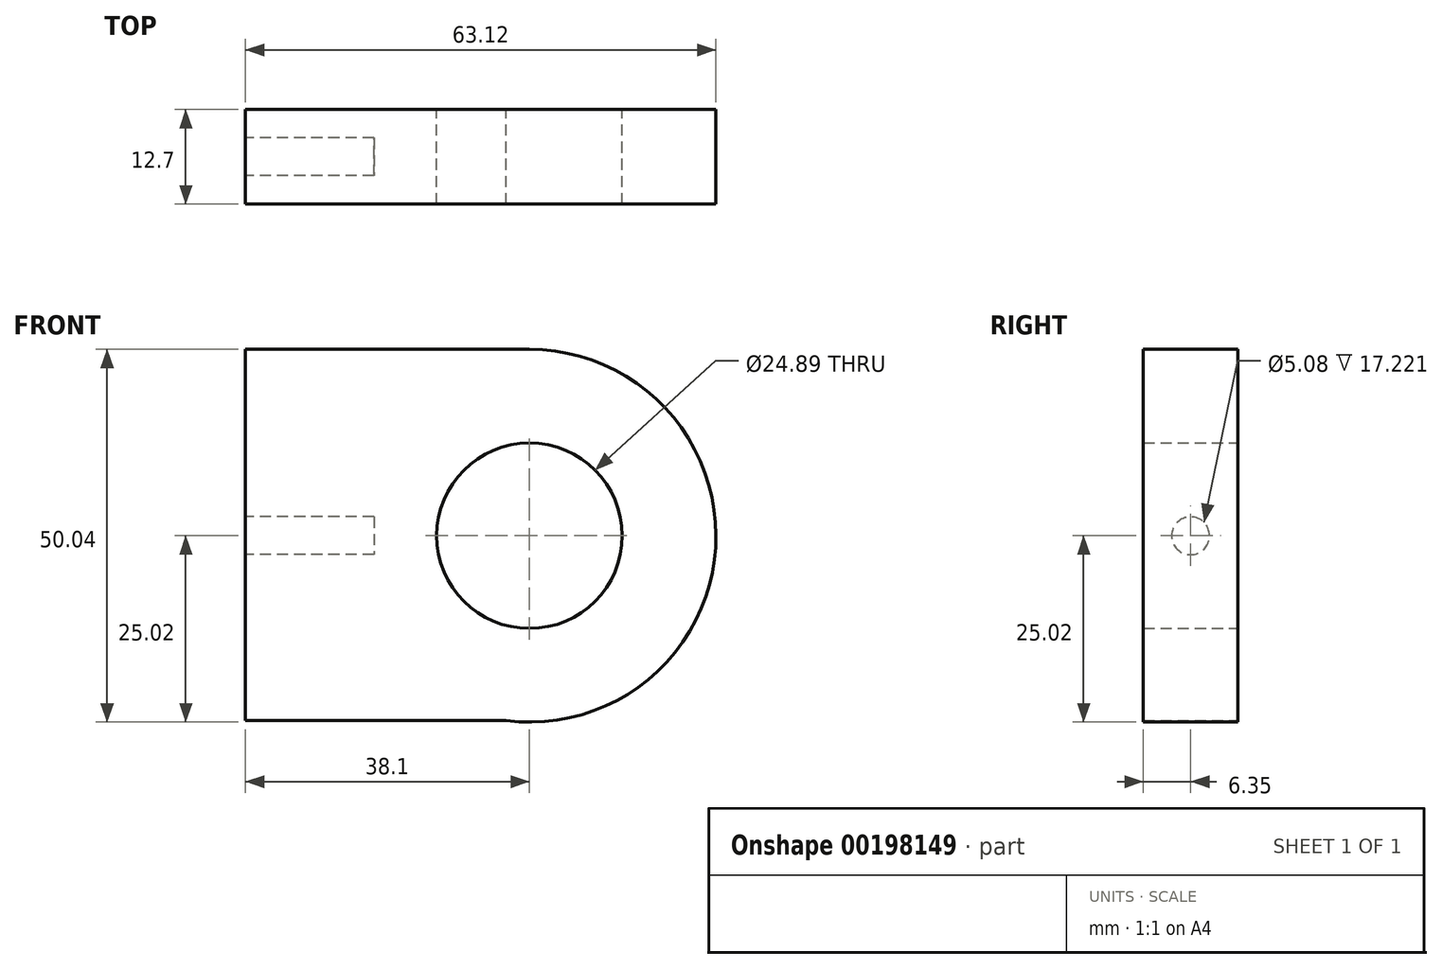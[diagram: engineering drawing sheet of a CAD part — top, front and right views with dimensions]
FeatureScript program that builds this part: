
annotation { "Feature Type Name" : "Feature", "Feature Type Description" : "" }
export const myFeature = defineFeature(function(context is Context, id is Id, definition is map)
    precondition{}
    {
        {
            var Q0;
            Q0=qCreatedBy(makeId("Front.planeOp"),FACE);
            var sketch = newSketch(context, id + "F0", { "sketchPlane" : qUnion([Q0])});
            skCircle(sketch, "E0", {"center": v(0, 0) * mm, "radius": 12.45 * mm});
            skArc(sketch, "E1", {"start": v(-3.12, -24.82) * mm, "mid": v(24.97, -1.56) * mm, "end": v(0, 25.02) * mm});
            skLineSegment(sketch, "E2", {"start": v(0, 25.02) * mm, "end": v(-38.1, 25.02) * mm});
            skLineSegment(sketch, "E3", {"start": v(-38.1, 25.02) * mm, "end": v(-38.1, -24.82) * mm});
            skLineSegment(sketch, "E4", {"start": v(-38.1, -24.82) * mm, "end": v(-3.12, -24.82) * mm});
            skSolve(sketch);
        }
        {
            var Q0;
            Q0 = qSketchRegion(id + "F0", true);
            extrude(context, id + "F1", {"entities" : qUnion([Q0]), "depth" : 12.7 * mm});
        }
        {
            var Q0;
            Q0=makeQuery(id+"F1.opExtrude","SWEPT_FACE",FACE,{"disambiguationData":[OSD([sQuery(id+"F0.wireOp",EDGE,"E3")])]});
            var sketch = newSketch(context, id + "F2", { "sketchPlane" : qUnion([Q0])});
            skLineSegment(sketch, "E5", {"start": v(0, 0) * mm, "end": v(3.81, 0) * mm});
            skCircle(sketch, "E6", {"center": v(6.35, 0) * mm, "radius": 2.54 * mm});
            skLineSegment(sketch, "E7.trimOffspring", {"start": v(8.9, 0) * mm, "end": v(12.7, 0) * mm});
            skSolve(sketch);
        }
        {
            var Q0;
            Q0 = qSketchRegion(id + "F2", true);
            extrude(context, id + "F3", {"entities" : qUnion([Q0]), "operationType" : NewBodyOperationType.REMOVE, "oppositeDirection" : true, "depth" : 17.22 * mm});
        }
    });
